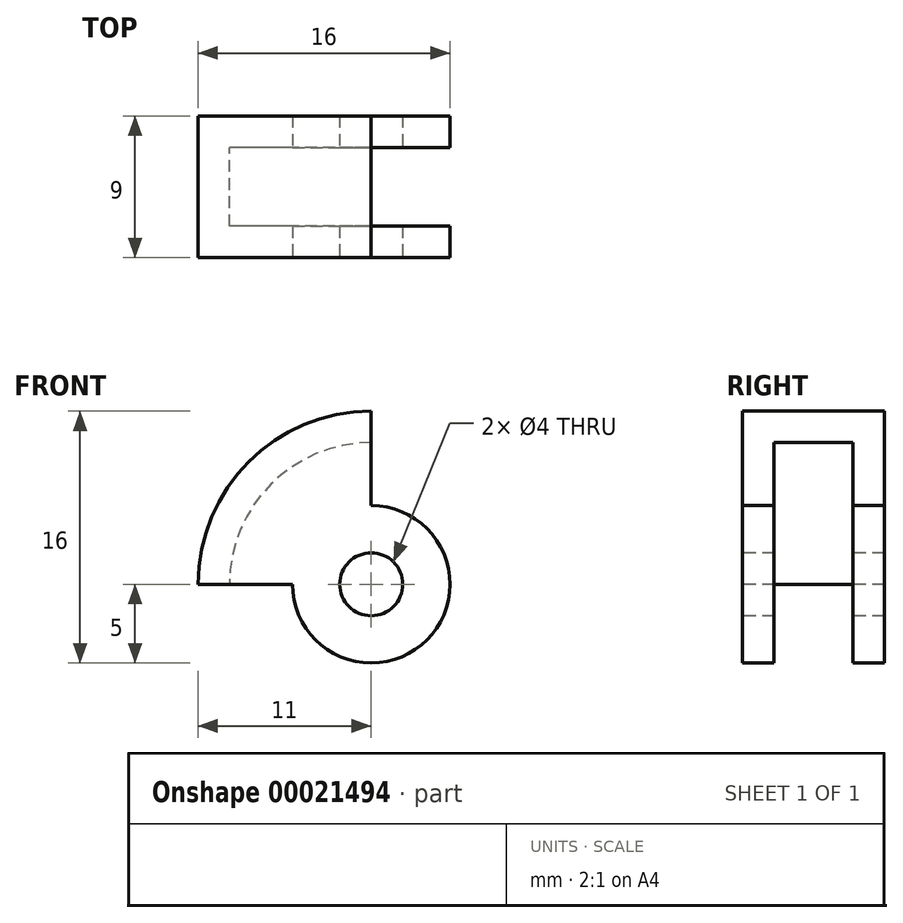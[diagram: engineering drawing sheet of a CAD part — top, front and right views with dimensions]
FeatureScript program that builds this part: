
annotation { "Feature Type Name" : "Feature", "Feature Type Description" : "" }
export const myFeature = defineFeature(function(context is Context, id is Id, definition is map)
    precondition{}
    {
        {
            var Q0;
            Q0=qCreatedBy(makeId("Front.planeOp"),FACE);
            var sketch = newSketch(context, id + "F0", { "sketchPlane" : qUnion([Q0])});
            skCircle(sketch, "E0", {"center": v(0, 0) * mm, "radius": 11 * mm});
            skSolve(sketch);
        }
        {
            var Q0;
            Q0=makeQuery(id+"F0.imprint","IMPRINT",FACE,{"disambiguationData":[TD([[makeQuery(id+"F0.imprint","IMPRINT",EDGE,{"derivedFrom":sQuery(id+"F0.wireOp",EDGE,"E0")}),1.0]])]});
            extrude(context, id + "F1", {"entities" : qUnion([Q0]), "depth" : 9 * mm});
        }
        {
            var Q0;
            Q0=makeQuery(id+"F1.opExtrude","CAP_FACE",FACE,{"disambiguationData":[OSD([sQuery(id+"F0.wireOp",EDGE,"E0")])],"isStart":false});
            var sketch = newSketch(context, id + "F2", { "sketchPlane" : qUnion([Q0])});
            skCircle(sketch, "E1", {"center": v(0, 0) * mm, "radius": 5 * mm});
            skLineSegment(sketch, "E2", {"start": v(0, 0) * mm, "end": v(-11, 0) * mm});
            skLineSegment(sketch, "E3", {"start": v(0, 0) * mm, "end": v(0, 11) * mm});
            skCircle(sketch, "E4", {"center": v(0, 0) * mm, "radius": 2 * mm});
            skSolve(sketch);
        }
        {
            var Q0;
            {var subQ0=sQuery(id+"F2.wireOp",EDGE,"E2");var subQ1=sQuery(id+"F2.wireOp",EDGE,"E1");var subQ2=makeQuery(id+"F2.imprint","INTERSECT",VERTEX,{"derivedFrom":[subQ1,subQ0]});Q0=makeQuery(id+"F2.imprint","IMPRINT",FACE,{"disambiguationData":[TD([[makeQuery(id+"F2.imprint","IMPRINT",EDGE,{"disambiguationData":[TD([[subQ2,-1.0]])],"derivedFrom":subQ1}),-1.0]])]});}
            extrude(context, id + "F3", {"entities" : qUnion([Q0]), "operationType" : NewBodyOperationType.REMOVE, "oppositeDirection" : true, "depth" : 25 * mm});
        }
        {
            var Q0;
            Q0=makeQuery(id+"F3.boolean.opBoolean","COPY",FACE,{"derivedFrom":makeQuery(id+"F3.opExtrude","SWEPT_FACE",FACE,{"disambiguationData":[OSD([sQuery(id+"F2.wireOp",EDGE,"E2")])]})});
            var Q1;
            Q1=makeQuery(id+"F3.boolean.opBoolean","COPY",FACE,{"derivedFrom":makeQuery(id+"F3.opExtrude","SWEPT_FACE",FACE,{"disambiguationData":[OSD([sQuery(id+"F2.wireOp",EDGE,"E1")])]})});
            var Q2;
            Q2=makeQuery(id+"F3.boolean.opBoolean","COPY",FACE,{"derivedFrom":makeQuery(id+"F3.opExtrude","SWEPT_FACE",FACE,{"disambiguationData":[OSD([sQuery(id+"F2.wireOp",EDGE,"E3")])]})});
            shell(context, id + "F4", {"entities" : qUnion([Q0, Q1, Q2]), "thickness" : 2 * mm});
        }
        {
            var Q0;
            {var subQ0=sQuery(id+"F2.wireOp",EDGE,"E3");var subQ1=sQuery(id+"F2.wireOp",EDGE,"E2");var subQ2=makeQuery(id+"F2.imprint","INTERSECT",VERTEX,{"derivedFrom":[subQ1,subQ0]});Q0=makeQuery(id+"F2.imprint","IMPRINT",FACE,{"disambiguationData":[TD([[makeQuery(id+"F2.imprint","IMPRINT",EDGE,{"disambiguationData":[TD([[subQ2,-1.0]])],"derivedFrom":subQ1}),1.0]])]});}
            var Q1;
            {var subQ0=sQuery(id+"F2.wireOp",EDGE,"E3");var subQ1=sQuery(id+"F2.wireOp",EDGE,"E2");var subQ2=makeQuery(id+"F2.imprint","INTERSECT",VERTEX,{"derivedFrom":[subQ1,subQ0]});Q1=makeQuery(id+"F2.imprint","IMPRINT",FACE,{"disambiguationData":[TD([[makeQuery(id+"F2.imprint","IMPRINT",EDGE,{"disambiguationData":[TD([[subQ2,-1.0]])],"derivedFrom":subQ1}),-1.0]])]});}
            extrude(context, id + "F5", {"entities" : qUnion([Q0, Q1]), "operationType" : NewBodyOperationType.REMOVE, "oppositeDirection" : true, "depth" : 25 * mm});
        }
    });
